SOLIDWORKS PART (.sldprt)
format: sldprt  version: not decoded by parser v0  size: 1,013,248 bytes
history: native  units: mm
features: plane x5, chamfer x4, sketch x2, material x1, extrude x1, cut_extrude x1 (+8 scaffold rows collapsed)
feature tree (22):
  scaffold x8  (default folders/planes/origin — collapsed)
  material  "Material <not specified>"
  plane  "Alzado"
  plane  "Planta"
  plane  "Vista lateral"
  sketch  "Croquis1"  dims[D1=60.0mm D2=8.0mm]
  extrude  "Extruir1"  Depth=9.5mm
  sketch  "Croquis2"  dims[D1=0.5mm D2=0.5mm D3=0.75mm D4=0.75mm]
  cut_extrude  "Cortar-Extruir1"  Depth=8.5mm
  chamfer  "Chaflán1"  Distance=0.5mm Angle=45deg
  chamfer  "Chaflán3"  Distance=0.5mm Angle=45deg
  chamfer  "Chaflán4"  Distance=0.5mm Angle=45deg
  chamfer  "Chaflán5"  Distance=0.5mm Angle=45deg
  plane  "Plano1"
  plane  "Plano2"
decode coverage: 8 of 8 modeling features carry decoded parameters
note: suppression state not decoded; provenance and decode notes live in map.json
